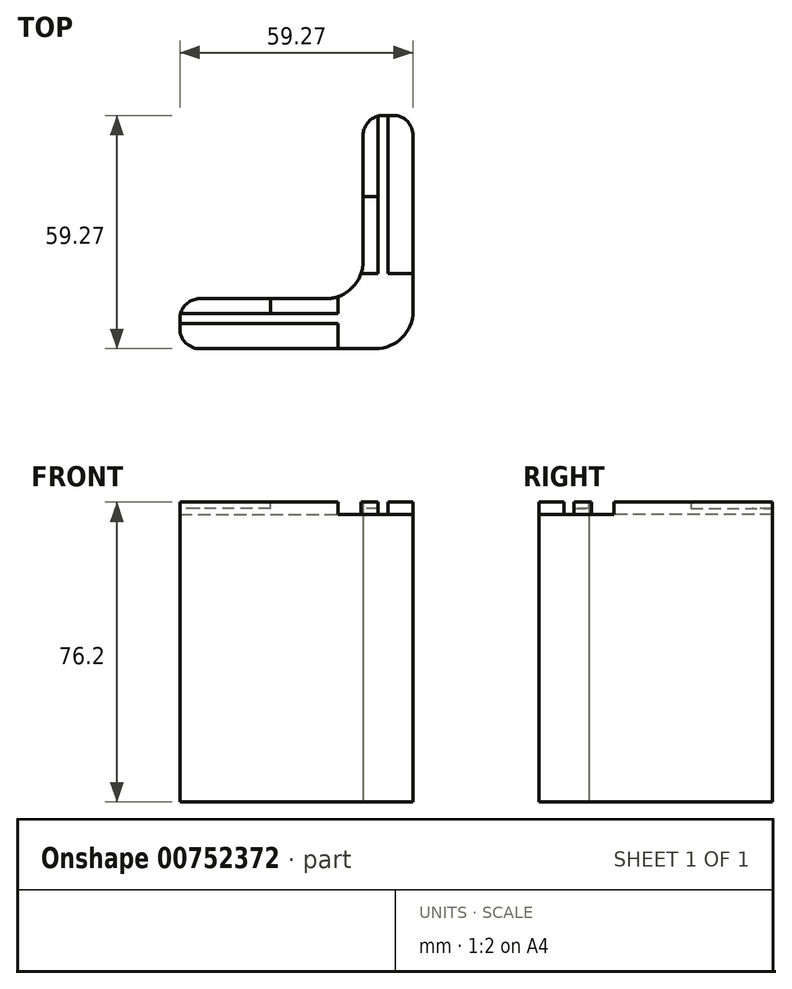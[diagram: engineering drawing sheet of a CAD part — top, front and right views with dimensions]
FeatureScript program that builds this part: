
annotation { "Feature Type Name" : "Feature", "Feature Type Description" : "" }
export const myFeature = defineFeature(function(context is Context, id is Id, definition is map)
    precondition{}
    {
        {
            var Q0;
            Q0=qCreatedBy(makeId("Top.planeOp"),FACE);
            var sketch = newSketch(context, id + "F0", { "sketchPlane" : qUnion([Q0])});
            skLineSegment(sketch, "E0.bottom", {"start": v(0, 0) * mm, "end": v(-12.7, 0) * mm});
            skLineSegment(sketch, "E0.top", {"start": v(0, 59.27) * mm, "end": v(-12.7, 59.27) * mm});
            skLineSegment(sketch, "E0.left", {"start": v(0, 0) * mm, "end": v(0, 59.27) * mm});
            skLineSegment(sketch, "E0.right", {"start": v(-12.7, 12.7) * mm, "end": v(-12.7, 59.27) * mm});
            skLineSegment(sketch, "E1.bottom", {"start": v(-12.7, 0) * mm, "end": v(-59.27, 0) * mm});
            skLineSegment(sketch, "E1.top", {"start": v(-12.7, 12.7) * mm, "end": v(-59.27, 12.7) * mm});
            skLineSegment(sketch, "E1.right", {"start": v(-59.27, 0) * mm, "end": v(-59.27, 12.7) * mm});
            skSolve(sketch);
        }
        {
            var Q0;
            Q0=makeQuery(id+"F0.imprint","IMPRINT",FACE,{"disambiguationData":[TD([[makeQuery(id+"F0.imprint","IMPRINT",EDGE,{"derivedFrom":sQuery(id+"F0.wireOp",EDGE,"E0.bottom")}),-1.0]])]});
            extrude(context, id + "F1", {"entities" : qUnion([Q0]), "depth" : 76.2 * mm, "offsetDistance" : 25.4 * mm});
        }
        {
            var Q0;
            Q0=makeQuery(id+"F1.opExtrude","SWEPT_EDGE",EDGE,{"disambiguationData":[OSD([sQuery(id+"F0.wireOp",EDGE,"E0.right"),sQuery(id+"F0.wireOp",EDGE,"E1.top")])]});
            var Q1;
            Q1=makeQuery(id+"F1.opExtrude","SWEPT_EDGE",EDGE,{"disambiguationData":[OSD([sQuery(id+"F0.wireOp",EDGE,"E0.bottom"),sQuery(id+"F0.wireOp",EDGE,"E0.left")])]});
            fillet(context, id + "F2", {"entities" : qUnion([Q0, Q1]), "radius" : 9.52 * mm, "tangentPropagation" : true, "allowEdgeOverflow" : false});
        }
        {
            var Q0;
            Q0=qCreatedBy(makeId("Top.planeOp"),FACE);
            cPlane(context, id + "F3", {"entities" : qUnion([Q0]), "cplaneType" : CPlaneType.OFFSET, "offset" : 76.2 * mm, "width" : 152.4 * mm, "height" : 152.4 * mm});
        }
        {
            var Q0;
            Q0=qCreatedBy(id+"F3.planeOp",FACE);
            var sketch = newSketch(context, id + "F4", { "sketchPlane" : qUnion([Q0])});
            skLineSegment(sketch, "E2.bottom", {"start": v(0, 0) * mm, "end": v(-19.05, 0) * mm});
            skLineSegment(sketch, "E2.top", {"start": v(0, 19.05) * mm, "end": v(-19.05, 19.05) * mm});
            skLineSegment(sketch, "E2.left", {"start": v(0, 0) * mm, "end": v(0, 19.05) * mm});
            skLineSegment(sketch, "E2.right", {"start": v(-19.05, 0) * mm, "end": v(-19.05, 19.05) * mm});
            skSolve(sketch);
        }
        {
            var Q0;
            Q0=makeQuery(id+"F4.imprint","IMPRINT",FACE,{"disambiguationData":[TD([[makeQuery(id+"F4.imprint","IMPRINT",EDGE,{"derivedFrom":sQuery(id+"F4.wireOp",EDGE,"E2.bottom")}),-1.0]])]});
            extrude(context, id + "F5", {"entities" : qUnion([Q0]), "operationType" : NewBodyOperationType.REMOVE, "oppositeDirection" : true, "depth" : 3.17 * mm, "offsetDistance" : 25.4 * mm});
        }
        {
            var Q0;
            Q0=qCreatedBy(id+"F3.planeOp",FACE);
            var sketch = newSketch(context, id + "F6", { "sketchPlane" : qUnion([Q0])});
            skLineSegment(sketch, "E3.bottom", {"start": v(-6.35, 62.28) * mm, "end": v(-8.9, 62.28) * mm});
            skLineSegment(sketch, "E3.top", {"start": v(-6.35, 17.83) * mm, "end": v(-8.9, 17.83) * mm});
            skLineSegment(sketch, "E3.left", {"start": v(-6.35, 62.28) * mm, "end": v(-6.35, 17.83) * mm});
            skLineSegment(sketch, "E3.right", {"start": v(-8.9, 62.28) * mm, "end": v(-8.9, 17.83) * mm});
            skLineSegment(sketch, "E4.bottom", {"start": v(-62.13, 6.35) * mm, "end": v(-17.68, 6.35) * mm});
            skLineSegment(sketch, "E4.top", {"start": v(-62.13, 8.9) * mm, "end": v(-17.68, 8.9) * mm});
            skLineSegment(sketch, "E4.left", {"start": v(-62.13, 6.35) * mm, "end": v(-62.13, 8.9) * mm});
            skLineSegment(sketch, "E4.right", {"start": v(-17.68, 6.35) * mm, "end": v(-17.68, 8.9) * mm});
            skSolve(sketch);
        }
        {
            var Q0;
            Q0=makeQuery(id+"F6.imprint","IMPRINT",FACE,{"disambiguationData":[TD([[makeQuery(id+"F6.imprint","IMPRINT",EDGE,{"derivedFrom":sQuery(id+"F6.wireOp",EDGE,"E3.bottom")}),1.0]])]});
            var Q1;
            Q1=makeQuery(id+"F6.imprint","IMPRINT",FACE,{"disambiguationData":[TD([[makeQuery(id+"F6.imprint","IMPRINT",EDGE,{"derivedFrom":sQuery(id+"F6.wireOp",EDGE,"E4.bottom")}),1.0]])]});
            extrude(context, id + "F7", {"entities" : qUnion([Q0, Q1]), "operationType" : NewBodyOperationType.REMOVE, "oppositeDirection" : true, "depth" : 3.17 * mm, "offsetDistance" : 25.4 * mm});
        }
        {
            var Q0;
            Q0=makeQuery(id+"F1.opExtrude","SWEPT_EDGE",EDGE,{"disambiguationData":[OSD([sQuery(id+"F0.wireOp",EDGE,"E1.bottom"),sQuery(id+"F0.wireOp",EDGE,"E1.right")])]});
            var Q1;
            Q1=makeQuery(id+"F1.opExtrude","SWEPT_EDGE",EDGE,{"disambiguationData":[OSD([sQuery(id+"F0.wireOp",EDGE,"E1.top"),sQuery(id+"F0.wireOp",EDGE,"E1.right")])]});
            var Q2;
            Q2=makeQuery(id+"F1.opExtrude","SWEPT_EDGE",EDGE,{"disambiguationData":[OSD([sQuery(id+"F0.wireOp",EDGE,"E0.top"),sQuery(id+"F0.wireOp",EDGE,"E0.right")])]});
            var Q3;
            Q3=makeQuery(id+"F1.opExtrude","SWEPT_EDGE",EDGE,{"disambiguationData":[OSD([sQuery(id+"F0.wireOp",EDGE,"E0.top"),sQuery(id+"F0.wireOp",EDGE,"E0.left")])]});
            fillet(context, id + "F8", {"entities" : qUnion([Q0, Q1, Q2, Q3]), "radius" : 5.08 * mm, "tangentPropagation" : true, "allowEdgeOverflow" : false});
        }
        {
            var Q0;
            Q0=qCreatedBy(id+"F3.planeOp",FACE);
            var sketch = newSketch(context, id + "F9", { "sketchPlane" : qUnion([Q0])});
            skLineSegment(sketch, "E5.bottom", {"start": v(-61.12, 7.85) * mm, "end": v(-36.26, 7.85) * mm});
            skLineSegment(sketch, "E5.top", {"start": v(-61.12, 15.3) * mm, "end": v(-36.26, 15.3) * mm});
            skLineSegment(sketch, "E5.left", {"start": v(-61.12, 7.85) * mm, "end": v(-61.12, 15.3) * mm});
            skLineSegment(sketch, "E5.right", {"start": v(-36.26, 7.85) * mm, "end": v(-36.26, 15.3) * mm});
            skLineSegment(sketch, "E6.bottom", {"start": v(-7.26, 61.62) * mm, "end": v(-16.33, 61.62) * mm});
            skLineSegment(sketch, "E6.top", {"start": v(-7.26, 38.6) * mm, "end": v(-16.33, 38.6) * mm});
            skLineSegment(sketch, "E6.left", {"start": v(-7.26, 61.62) * mm, "end": v(-7.26, 38.6) * mm});
            skLineSegment(sketch, "E6.right", {"start": v(-16.33, 61.62) * mm, "end": v(-16.33, 38.6) * mm});
            skSolve(sketch);
        }
        {
            var Q0;
            Q0=makeQuery(id+"F9.imprint","IMPRINT",FACE,{"disambiguationData":[TD([[makeQuery(id+"F9.imprint","IMPRINT",EDGE,{"derivedFrom":sQuery(id+"F9.wireOp",EDGE,"E5.bottom")}),1.0]])]});
            var Q1;
            Q1=makeQuery(id+"F9.imprint","IMPRINT",FACE,{"disambiguationData":[TD([[makeQuery(id+"F9.imprint","IMPRINT",EDGE,{"derivedFrom":sQuery(id+"F9.wireOp",EDGE,"E6.bottom")}),1.0]])]});
            extrude(context, id + "F10", {"entities" : qUnion([Q0, Q1]), "operationType" : NewBodyOperationType.REMOVE, "oppositeDirection" : true, "depth" : 1.59 * mm, "offsetDistance" : 25.4 * mm});
        }
    });
